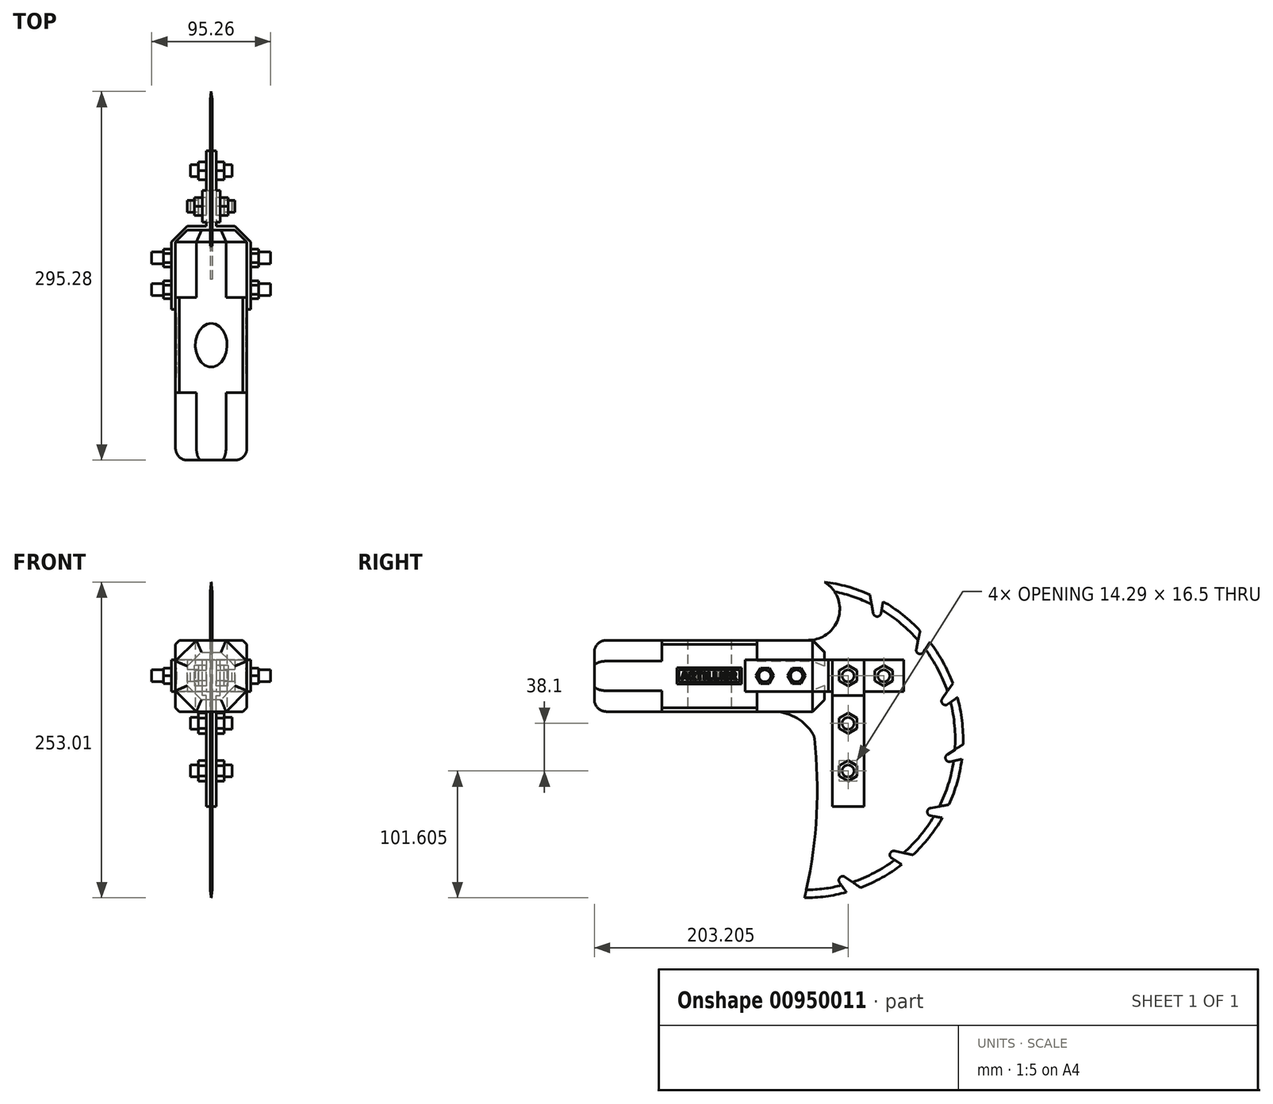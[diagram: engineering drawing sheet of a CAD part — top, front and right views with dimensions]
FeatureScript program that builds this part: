
annotation { "Feature Type Name" : "Feature", "Feature Type Description" : "" }
export const myFeature = defineFeature(function(context is Context, id is Id, definition is map)
    precondition{}
    {
        {
            var Q0;
            Q0=qCreatedBy(makeId("Top.planeOp"),FACE);
            var sketch = newSketch(context, id + "F0", { "sketchPlane" : qUnion([Q0])});
            skEllipse(sketch, "E0", {"center": v(0, 0) * mm, "majorRadius": 12.7 * mm, "minorRadius": 17.46 * mm, "majorAxis": v(1, 0)});
            skSolve(sketch);
        }
        {
            var Q0;
            Q0 = qSketchRegion(id + "F0", true);
            extrude(context, id + "F1", {"entities" : qUnion([Q0]), "depth" : 1219.2 * mm, "offsetDistance" : 25.4 * mm});
        }
        {
            var Q0;
            Q0=qCreatedBy(makeId("Front.planeOp"),FACE);
            var sketch = newSketch(context, id + "F2", { "sketchPlane" : qUnion([Q0])});
            skCircle(sketch, "E1.cCircle", {"center": v(0, 1177.87) * mm, "radius": 30.93 * mm, "construction": true});
            skLineSegment(sketch, "E1.0", {"start": v(28.57, 1189.7) * mm, "end": v(28.57, 1166.03) * mm});
            skLineSegment(sketch, "E1.1", {"start": v(28.57, 1166.03) * mm, "end": v(11.84, 1149.3) * mm});
            skLineSegment(sketch, "E1.2", {"start": v(11.84, 1149.3) * mm, "end": v(-11.84, 1149.3) * mm});
            skLineSegment(sketch, "E1.3", {"start": v(-11.84, 1149.3) * mm, "end": v(-28.58, 1166.03) * mm});
            skLineSegment(sketch, "E1.4", {"start": v(-28.58, 1166.03) * mm, "end": v(-28.58, 1189.7) * mm});
            skLineSegment(sketch, "E1.5", {"start": v(-28.57, 1189.7) * mm, "end": v(-11.84, 1206.44) * mm});
            skLineSegment(sketch, "E1.6", {"start": v(-11.84, 1206.44) * mm, "end": v(11.84, 1206.44) * mm});
            skLineSegment(sketch, "E1.7", {"start": v(11.84, 1206.44) * mm, "end": v(28.57, 1189.7) * mm});
            skLineSegment(sketch, "E2.bottom", {"start": v(28.57, 1206.44) * mm, "end": v(-28.58, 1206.44) * mm});
            skLineSegment(sketch, "E2.top", {"start": v(28.57, 1149.3) * mm, "end": v(-28.58, 1149.3) * mm});
            skLineSegment(sketch, "E2.left", {"start": v(28.57, 1206.44) * mm, "end": v(28.57, 1149.3) * mm});
            skLineSegment(sketch, "E2.right", {"start": v(-28.58, 1206.44) * mm, "end": v(-28.58, 1149.3) * mm});
            skSolve(sketch);
        }
        {
            var Q0;
            {var subQ0=sQuery(id+"F2.wireOp",EDGE,"E1.5");Q0=makeQuery(id+"F2.imprint","IMPRINT",FACE,{"disambiguationData":[TD([[makeQuery(id+"F2.imprint","IMPRINT",EDGE,{"derivedFrom":subQ0}),1.0]])]});}
            var Q1;
            {var subQ0=sQuery(id+"F2.wireOp",EDGE,"E1.7");Q1=makeQuery(id+"F2.imprint","IMPRINT",FACE,{"disambiguationData":[TD([[makeQuery(id+"F2.imprint","IMPRINT",EDGE,{"derivedFrom":subQ0}),1.0]])]});}
            var Q2;
            Q2=makeQuery(id+"F2.imprint","IMPRINT",FACE,{"disambiguationData":[TD([[makeQuery(id+"F2.imprint","IMPRINT",EDGE,{"derivedFrom":sQuery(id+"F2.wireOp",EDGE,"E1.0")}),-1.0]])]});
            var Q3;
            {var subQ0=sQuery(id+"F2.wireOp",EDGE,"E1.3");Q3=makeQuery(id+"F2.imprint","IMPRINT",FACE,{"disambiguationData":[TD([[makeQuery(id+"F2.imprint","IMPRINT",EDGE,{"derivedFrom":subQ0}),1.0]])]});}
            var Q4;
            {var subQ0=sQuery(id+"F2.wireOp",EDGE,"E1.1");Q4=makeQuery(id+"F2.imprint","IMPRINT",FACE,{"disambiguationData":[TD([[makeQuery(id+"F2.imprint","IMPRINT",EDGE,{"derivedFrom":subQ0}),1.0]])]});}
            extrude(context, id + "F3", {"entities" : qUnion([Q0, Q1, Q2, Q3, Q4]), "depth" : 38.1 * mm, "offsetDistance" : 25.4 * mm, "hasSecondDirection" : true, "secondDirectionOppositeDirection" : true, "secondDirectionDepth" : 38.1 * mm});
        }
        {
            var Q0;
            Q0=makeQuery(id+"F2.imprint","IMPRINT",FACE,{"disambiguationData":[TD([[makeQuery(id+"F2.imprint","IMPRINT",EDGE,{"derivedFrom":sQuery(id+"F2.wireOp",EDGE,"E1.0")}),-1.0]])]});
            extrude(context, id + "F4", {"entities" : qUnion([Q0]), "operationType" : NewBodyOperationType.ADD, "depth" : 92.07 * mm, "offsetDistance" : 25.4 * mm, "hasSecondDirection" : true, "secondDirectionOppositeDirection" : true, "secondDirectionDepth" : 92.07 * mm});
        }
        {
            var Q0;
            Q0=makeQuery(id+"F4.opExtrude","CAP_EDGE",EDGE,{"disambiguationData":[OSD([sQuery(id+"F2.wireOp",EDGE,"E1.1")])],"isStart":true});
            var Q1;
            Q1=makeQuery(id+"F4.opExtrude","CAP_EDGE",EDGE,{"disambiguationData":[OSD([sQuery(id+"F2.wireOp",EDGE,"E1.0")])],"isStart":true});
            var Q2;
            Q2=makeQuery(id+"F4.opExtrude","CAP_EDGE",EDGE,{"disambiguationData":[OSD([sQuery(id+"F2.wireOp",EDGE,"E1.7")])],"isStart":true});
            var Q3;
            Q3=makeQuery(id+"F4.opExtrude","CAP_EDGE",EDGE,{"disambiguationData":[OSD([sQuery(id+"F2.wireOp",EDGE,"E1.3")])],"isStart":true});
            var Q4;
            Q4=makeQuery(id+"F4.opExtrude","CAP_EDGE",EDGE,{"disambiguationData":[OSD([sQuery(id+"F2.wireOp",EDGE,"E1.5")])],"isStart":true});
            var Q5;
            Q5=makeQuery(id+"F4.opExtrude","CAP_EDGE",EDGE,{"disambiguationData":[OSD([sQuery(id+"F2.wireOp",EDGE,"E1.4")])],"isStart":true});
            var Q6;
            Q6=makeQuery(id+"F4.opExtrude","CAP_EDGE",EDGE,{"disambiguationData":[OSD([sQuery(id+"F2.wireOp",EDGE,"E1.6")])],"isStart":true});
            var Q7;
            Q7=makeQuery(id+"F4.opExtrude","CAP_EDGE",EDGE,{"disambiguationData":[OSD([sQuery(id+"F2.wireOp",EDGE,"E1.2")])],"isStart":true});
            chamfer(context, id + "F5", {"entities" : qUnion([Q0, Q1, Q2, Q3, Q4, Q5, Q6, Q7]), "width" : 9.52 * mm, "tangentPropagation" : true});
        }
        {
            var Q0;
            Q0=makeQuery(id+"F4.opExtrude","CAP_FACE",FACE,{"disambiguationData":[OSD([sQuery(id+"F2.wireOp",EDGE,"E1.0"),sQuery(id+"F2.wireOp",EDGE,"E1.1"),sQuery(id+"F2.wireOp",EDGE,"E1.2"),sQuery(id+"F2.wireOp",EDGE,"E1.3"),sQuery(id+"F2.wireOp",EDGE,"E1.4"),sQuery(id+"F2.wireOp",EDGE,"E1.5"),sQuery(id+"F2.wireOp",EDGE,"E1.6"),sQuery(id+"F2.wireOp",EDGE,"E1.7")])],"isStart":false});
            fillet(context, id + "F6", {"entities" : qUnion([Q0]), "radius" : 9.52 * mm, "tangentPropagation" : true, "allowEdgeOverflow" : false});
        }
        {
            var Q0;
            Q0=qCreatedBy(makeId("Right.planeOp"),FACE);
            var sketch = newSketch(context, id + "F7", { "sketchPlane" : qUnion([Q0])});
            skPoint(sketch, "E3", {"position": v(38.1, 1177.93) * mm});
            skPoint(sketch, "E4", {"position": v(92.07, 1177.93) * mm});
            skCircle(sketch, "E5", {"center": v(76.2, 1127.13) * mm, "radius": 127 * mm});
            skCircle(sketch, "E6", {"center": v(76.2, 1127.13) * mm, "radius": 7.94 * mm});
            skLineSegment(sketch, "E7.bottom", {"start": v(38.1, 1149.35) * mm, "end": v(82.55, 1149.35) * mm});
            skLineSegment(sketch, "E7.top", {"start": v(38.1, 1206.5) * mm, "end": v(82.55, 1206.5) * mm});
            skLineSegment(sketch, "E7.left", {"start": v(38.1, 1149.35) * mm, "end": v(38.1, 1206.5) * mm});
            skLineSegment(sketch, "E7.right", {"start": v(92.07, 1149.35) * mm, "end": v(92.07, 1206.5) * mm});
            skPoint(sketch, "E7.middle", {"position": v(65.09, 1177.93) * mm});
            skArc(sketch, "E8", {"start": v(79.37, 1206.5) * mm, "mid": v(103.54, 1224.96) * mm, "end": v(92.07, 1253.13) * mm});
            skArc(sketch, "E9", {"start": v(82.98, 1131.25) * mm, "mid": v(69.26, 1144.51) * mm, "end": v(50.8, 1149.35) * mm});
            skArc(sketch, "E10", {"start": v(76.2, 1000.13) * mm, "mid": v(85.65, 1063.72) * mm, "end": v(84.09, 1128) * mm});
            skLineSegment(sketch, "E11", {"start": v(76.2, 1127.13) * mm, "end": v(92.07, 1253.13) * mm, "construction": true});
            skLineSegment(sketch, "E12", {"start": v(76.2, 1127.13) * mm, "end": v(139.09, 1237.46) * mm, "construction": true});
            skLineSegment(sketch, "E13", {"start": v(76.2, 1127.13) * mm, "end": v(176.52, 1205) * mm, "construction": true});
            skLineSegment(sketch, "E14", {"start": v(76.2, 1127.13) * mm, "end": v(198.69, 1160.68) * mm, "construction": true});
            skLineSegment(sketch, "E15", {"start": v(76.2, 1127.13) * mm, "end": v(202.2, 1111.25) * mm, "construction": true});
            skLineSegment(sketch, "E16", {"start": v(76.2, 1127.13) * mm, "end": v(186.54, 1064.24) * mm, "construction": true});
            skLineSegment(sketch, "E17", {"start": v(76.2, 1127.13) * mm, "end": v(154.07, 1026.8) * mm, "construction": true});
            skLineSegment(sketch, "E18", {"start": v(109.75, 1004.64) * mm, "end": v(76.2, 1127.13) * mm, "construction": true});
            skLineSegment(sketch, "E19", {"start": v(139.09, 1237.46) * mm, "end": v(137.48, 1228.07) * mm});
            skLineSegment(sketch, "E20", {"start": v(176.52, 1205) * mm, "end": v(171.45, 1196.94) * mm});
            skLineSegment(sketch, "E21", {"start": v(198.69, 1160.68) * mm, "end": v(190.92, 1155.17) * mm});
            skLineSegment(sketch, "E22", {"start": v(202.2, 1111.25) * mm, "end": v(192.92, 1109.14) * mm});
            skLineSegment(sketch, "E23", {"start": v(186.54, 1064.24) * mm, "end": v(177.15, 1065.84) * mm});
            skLineSegment(sketch, "E24", {"start": v(154.07, 1026.8) * mm, "end": v(146.01, 1031.87) * mm});
            skLineSegment(sketch, "E25", {"start": v(109.75, 1004.64) * mm, "end": v(104.25, 1012.4) * mm});
            skArc(sketch, "E26", {"start": v(137.48, 1228.07) * mm, "mid": v(134.37, 1225.43) * mm, "end": v(131.23, 1228.04) * mm});
            skLineSegment(sketch, "E27", {"start": v(131.23, 1228.04) * mm, "end": v(128.54, 1242.84) * mm});
            skArc(sketch, "E28", {"start": v(171.45, 1196.94) * mm, "mid": v(167.56, 1195.69) * mm, "end": v(165.66, 1199.3) * mm});
            skLineSegment(sketch, "E29", {"start": v(165.66, 1199.3) * mm, "end": v(168.83, 1214) * mm});
            skArc(sketch, "E30", {"start": v(190.92, 1155.17) * mm, "mid": v(186.85, 1155.5) * mm, "end": v(186.47, 1159.57) * mm});
            skLineSegment(sketch, "E31", {"start": v(186.47, 1159.57) * mm, "end": v(195.03, 1171.94) * mm});
            skArc(sketch, "E32", {"start": v(192.92, 1109.14) * mm, "mid": v(189.29, 1111) * mm, "end": v(190.5, 1114.9) * mm});
            skLineSegment(sketch, "E33", {"start": v(190.5, 1114.9) * mm, "end": v(203.13, 1123.06) * mm});
            skArc(sketch, "E34", {"start": v(177.15, 1065.84) * mm, "mid": v(174.5, 1068.95) * mm, "end": v(177.11, 1072.1) * mm});
            skArc(sketch, "E35", {"start": v(146.01, 1031.87) * mm, "mid": v(144.76, 1035.76) * mm, "end": v(148.37, 1037.67) * mm});
            skArc(sketch, "E36", {"start": v(104.25, 1012.4) * mm, "mid": v(104.58, 1016.48) * mm, "end": v(108.64, 1016.86) * mm});
            skLineSegment(sketch, "E37", {"start": v(108.64, 1016.86) * mm, "end": v(121.02, 1008.3) * mm});
            skLineSegment(sketch, "E38", {"start": v(148.37, 1037.67) * mm, "end": v(163.08, 1034.5) * mm});
            skLineSegment(sketch, "E39", {"start": v(177.11, 1072.1) * mm, "end": v(191.91, 1074.79) * mm});
            skLineSegment(sketch, "E40", {"start": v(82.55, 1206.5) * mm, "end": v(92.07, 1196.98) * mm});
            skLineSegment(sketch, "E41", {"start": v(82.55, 1149.35) * mm, "end": v(92.08, 1158.88) * mm});
            skSolve(sketch);
        }
        {
            var Q0;
            {var subQ9=sQuery(id+"F7.wireOp",EDGE,"E8");Q0=makeQuery(id+"F7.imprint","IMPRINT",FACE,{"disambiguationData":[TD([[makeQuery(id+"F7.imprint","IMPRINT",EDGE,{"derivedFrom":subQ9}),-1.0]])]});}
            extrude(context, id + "F8", {"entities" : qUnion([Q0]), "depth" : 0.8 * mm, "offsetDistance" : 25.4 * mm, "hasSecondDirection" : true, "secondDirectionOppositeDirection" : true, "secondDirectionDepth" : 0.8 * mm});
        }
        {
            var Q0;
            {var subQ0=sQuery(id+"F7.wireOp",EDGE,"E5");Q0=makeQuery(id+"F8.opExtrude","CAP_EDGE",EDGE,{"disambiguationData":[OSD([subQ0]),TDD([makeQuery(id+"F7.imprint","IMPRINT",EDGE,{"disambiguationData":[TD([[makeQuery(id+"F7.imprint","INTERSECT",VERTEX,{"derivedFrom":[subQ0,sQuery(id+"F7.wireOp",EDGE,"E10")]}),-1.0]])],"derivedFrom":subQ0})])],"isStart":true});}
            var Q1;
            {var subQ0=sQuery(id+"F7.wireOp",EDGE,"E5");Q1=makeQuery(id+"F8.opExtrude","CAP_EDGE",EDGE,{"disambiguationData":[OSD([subQ0]),TDD([makeQuery(id+"F7.imprint","IMPRINT",EDGE,{"disambiguationData":[TD([[makeQuery(id+"F7.imprint","INTERSECT",VERTEX,{"derivedFrom":[subQ0,sQuery(id+"F7.wireOp",EDGE,"E22")]}),1.0]])],"derivedFrom":subQ0})])],"isStart":true});}
            var Q2;
            {var subQ0=sQuery(id+"F7.wireOp",EDGE,"E5");Q2=makeQuery(id+"F8.opExtrude","CAP_EDGE",EDGE,{"disambiguationData":[OSD([subQ0]),TDD([makeQuery(id+"F7.imprint","IMPRINT",EDGE,{"disambiguationData":[TD([[makeQuery(id+"F7.imprint","INTERSECT",VERTEX,{"derivedFrom":[subQ0,sQuery(id+"F7.wireOp",EDGE,"E21")]}),1.0]])],"derivedFrom":subQ0})])],"isStart":true});}
            var Q3;
            {var subQ0=sQuery(id+"F7.wireOp",EDGE,"E5");Q3=makeQuery(id+"F8.opExtrude","CAP_EDGE",EDGE,{"disambiguationData":[OSD([subQ0]),TDD([makeQuery(id+"F7.imprint","IMPRINT",EDGE,{"disambiguationData":[TD([[makeQuery(id+"F7.imprint","INTERSECT",VERTEX,{"derivedFrom":[subQ0,sQuery(id+"F7.wireOp",EDGE,"E20")]}),1.0]])],"derivedFrom":subQ0})])],"isStart":true});}
            var Q4;
            {var subQ0=sQuery(id+"F7.wireOp",EDGE,"E5");Q4=makeQuery(id+"F8.opExtrude","CAP_EDGE",EDGE,{"disambiguationData":[OSD([subQ0]),TDD([makeQuery(id+"F7.imprint","IMPRINT",EDGE,{"disambiguationData":[TD([[makeQuery(id+"F7.imprint","INTERSECT",VERTEX,{"derivedFrom":[subQ0,sQuery(id+"F7.wireOp",EDGE,"E19")]}),1.0]])],"derivedFrom":subQ0})])],"isStart":true});}
            var Q5;
            {var subQ0=sQuery(id+"F7.wireOp",EDGE,"E5");Q5=makeQuery(id+"F8.opExtrude","CAP_EDGE",EDGE,{"disambiguationData":[OSD([subQ0]),TDD([makeQuery(id+"F7.imprint","IMPRINT",EDGE,{"disambiguationData":[TD([[makeQuery(id+"F7.imprint","INTERSECT",VERTEX,{"derivedFrom":[subQ0,sQuery(id+"F7.wireOp",EDGE,"E8")]}),1.0]])],"derivedFrom":subQ0})])],"isStart":true});}
            var Q6;
            {var subQ0=sQuery(id+"F7.wireOp",EDGE,"E5");Q6=makeQuery(id+"F8.opExtrude","CAP_EDGE",EDGE,{"disambiguationData":[OSD([subQ0]),TDD([makeQuery(id+"F7.imprint","IMPRINT",EDGE,{"disambiguationData":[TD([[makeQuery(id+"F7.imprint","INTERSECT",VERTEX,{"derivedFrom":[subQ0,sQuery(id+"F7.wireOp",EDGE,"E24")]}),1.0]])],"derivedFrom":subQ0})])],"isStart":true});}
            var Q7;
            {var subQ0=sQuery(id+"F7.wireOp",EDGE,"E5");Q7=makeQuery(id+"F8.opExtrude","CAP_EDGE",EDGE,{"disambiguationData":[OSD([subQ0]),TDD([makeQuery(id+"F7.imprint","IMPRINT",EDGE,{"disambiguationData":[TD([[makeQuery(id+"F7.imprint","INTERSECT",VERTEX,{"derivedFrom":[subQ0,sQuery(id+"F7.wireOp",EDGE,"E23")]}),1.0]])],"derivedFrom":subQ0})])],"isStart":true});}
            chamfer(context, id + "F9", {"entities" : qUnion([Q0, Q1, Q2, Q3, Q4, Q5, Q6, Q7]), "chamferType" : ChamferType.TWO_OFFSETS, "width1" : 0.8 * mm, "oppositeDirection" : false, "width2" : 6.35 * mm, "tangentPropagation" : true});
        }
        {
            var Q0;
            {var subQ0=sQuery(id+"F7.wireOp",EDGE,"E5");Q0=makeQuery(id+"F8.opExtrude","CAP_EDGE",EDGE,{"disambiguationData":[OSD([subQ0]),TDD([makeQuery(id+"F7.imprint","IMPRINT",EDGE,{"disambiguationData":[TD([[makeQuery(id+"F7.imprint","INTERSECT",VERTEX,{"derivedFrom":[subQ0,sQuery(id+"F7.wireOp",EDGE,"E10")]}),-1.0]])],"derivedFrom":subQ0})])],"isStart":false});}
            var Q1;
            {var subQ0=sQuery(id+"F7.wireOp",EDGE,"E5");Q1=makeQuery(id+"F8.opExtrude","CAP_EDGE",EDGE,{"disambiguationData":[OSD([subQ0]),TDD([makeQuery(id+"F7.imprint","IMPRINT",EDGE,{"disambiguationData":[TD([[makeQuery(id+"F7.imprint","INTERSECT",VERTEX,{"derivedFrom":[subQ0,sQuery(id+"F7.wireOp",EDGE,"E23")]}),1.0]])],"derivedFrom":subQ0})])],"isStart":false});}
            var Q2;
            {var subQ0=sQuery(id+"F7.wireOp",EDGE,"E5");Q2=makeQuery(id+"F8.opExtrude","CAP_EDGE",EDGE,{"disambiguationData":[OSD([subQ0]),TDD([makeQuery(id+"F7.imprint","IMPRINT",EDGE,{"disambiguationData":[TD([[makeQuery(id+"F7.imprint","INTERSECT",VERTEX,{"derivedFrom":[subQ0,sQuery(id+"F7.wireOp",EDGE,"E22")]}),1.0]])],"derivedFrom":subQ0})])],"isStart":false});}
            var Q3;
            {var subQ0=sQuery(id+"F7.wireOp",EDGE,"E5");Q3=makeQuery(id+"F8.opExtrude","CAP_EDGE",EDGE,{"disambiguationData":[OSD([subQ0]),TDD([makeQuery(id+"F7.imprint","IMPRINT",EDGE,{"disambiguationData":[TD([[makeQuery(id+"F7.imprint","INTERSECT",VERTEX,{"derivedFrom":[subQ0,sQuery(id+"F7.wireOp",EDGE,"E21")]}),1.0]])],"derivedFrom":subQ0})])],"isStart":false});}
            var Q4;
            {var subQ0=sQuery(id+"F7.wireOp",EDGE,"E5");Q4=makeQuery(id+"F8.opExtrude","CAP_EDGE",EDGE,{"disambiguationData":[OSD([subQ0]),TDD([makeQuery(id+"F7.imprint","IMPRINT",EDGE,{"disambiguationData":[TD([[makeQuery(id+"F7.imprint","INTERSECT",VERTEX,{"derivedFrom":[subQ0,sQuery(id+"F7.wireOp",EDGE,"E20")]}),1.0]])],"derivedFrom":subQ0})])],"isStart":false});}
            var Q5;
            {var subQ0=sQuery(id+"F7.wireOp",EDGE,"E5");Q5=makeQuery(id+"F8.opExtrude","CAP_EDGE",EDGE,{"disambiguationData":[OSD([subQ0]),TDD([makeQuery(id+"F7.imprint","IMPRINT",EDGE,{"disambiguationData":[TD([[makeQuery(id+"F7.imprint","INTERSECT",VERTEX,{"derivedFrom":[subQ0,sQuery(id+"F7.wireOp",EDGE,"E19")]}),1.0]])],"derivedFrom":subQ0})])],"isStart":false});}
            var Q6;
            {var subQ0=sQuery(id+"F7.wireOp",EDGE,"E5");Q6=makeQuery(id+"F8.opExtrude","CAP_EDGE",EDGE,{"disambiguationData":[OSD([subQ0]),TDD([makeQuery(id+"F7.imprint","IMPRINT",EDGE,{"disambiguationData":[TD([[makeQuery(id+"F7.imprint","INTERSECT",VERTEX,{"derivedFrom":[subQ0,sQuery(id+"F7.wireOp",EDGE,"E8")]}),1.0]])],"derivedFrom":subQ0})])],"isStart":false});}
            var Q7;
            {var subQ0=sQuery(id+"F7.wireOp",EDGE,"E5");Q7=makeQuery(id+"F8.opExtrude","CAP_EDGE",EDGE,{"disambiguationData":[OSD([subQ0]),TDD([makeQuery(id+"F7.imprint","IMPRINT",EDGE,{"disambiguationData":[TD([[makeQuery(id+"F7.imprint","INTERSECT",VERTEX,{"derivedFrom":[subQ0,sQuery(id+"F7.wireOp",EDGE,"E24")]}),1.0]])],"derivedFrom":subQ0})])],"isStart":false});}
            chamfer(context, id + "F10", {"entities" : qUnion([Q0, Q1, Q2, Q3, Q4, Q5, Q6, Q7]), "chamferType" : ChamferType.TWO_OFFSETS, "width1" : 0.8 * mm, "oppositeDirection" : true, "width2" : 6.35 * mm, "tangentPropagation" : true});
        }
        {
            var Q0;
            Q0=makeQuery(id+"F3.opExtrude","SWEPT_EDGE",EDGE,{"disambiguationData":[OSD([sQuery(id+"F2.wireOp",EDGE,"E2.bottom"),sQuery(id+"F2.wireOp",EDGE,"E2.left")])]});
            var Q1;
            Q1=makeQuery(id+"F3.opExtrude","SWEPT_EDGE",EDGE,{"disambiguationData":[OSD([sQuery(id+"F2.wireOp",EDGE,"E2.top"),sQuery(id+"F2.wireOp",EDGE,"E2.left")])]});
            var Q2;
            Q2=makeQuery(id+"F3.opExtrude","SWEPT_EDGE",EDGE,{"disambiguationData":[OSD([sQuery(id+"F2.wireOp",EDGE,"E2.bottom"),sQuery(id+"F2.wireOp",EDGE,"E2.right")])]});
            var Q3;
            Q3=makeQuery(id+"F3.opExtrude","SWEPT_EDGE",EDGE,{"disambiguationData":[OSD([sQuery(id+"F2.wireOp",EDGE,"E2.top"),sQuery(id+"F2.wireOp",EDGE,"E2.right")])]});
            chamfer(context, id + "F11", {"entities" : qUnion([Q0, Q1, Q2, Q3]), "width" : 3.17 * mm, "tangentPropagation" : true});
        }
        {
            var Q0;
            Q0 = qSketchRegion(id + "F0", true);
            extrude(context, id + "F12", {"entities" : qUnion([Q0]), "operationType" : NewBodyOperationType.REMOVE, "depth" : 1219.2 * mm, "offsetDistance" : 25.4 * mm});
        }
        {
            var Q0;
            Q0=qCreatedBy(makeId("Top.planeOp"),FACE);
            var sketch = newSketch(context, id + "F13", { "sketchPlane" : qUnion([Q0])});
            skLineSegment(sketch, "E42.bottom", {"start": v(28.58, 28.58) * mm, "end": v(31.75, 28.58) * mm});
            skLineSegment(sketch, "E42.top", {"start": v(28.57, 82.55) * mm, "end": v(31.75, 82.55) * mm, "construction": true});
            skLineSegment(sketch, "E42.left", {"start": v(28.58, 28.58) * mm, "end": v(28.57, 82.55) * mm});
            skLineSegment(sketch, "E42.right", {"start": v(31.75, 28.58) * mm, "end": v(31.75, 82.55) * mm});
            skLineSegment(sketch, "E43", {"start": v(28.57, 82.55) * mm, "end": v(19.05, 92.08) * mm});
            skLineSegment(sketch, "E44", {"start": v(19.05, 92.08) * mm, "end": v(0.8, 92.08) * mm});
            skLineSegment(sketch, "E45", {"start": v(0.8, 92.08) * mm, "end": v(0.8, 155.58) * mm});
            skLineSegment(sketch, "E46", {"start": v(0.8, 155.58) * mm, "end": v(3.97, 155.58) * mm});
            skLineSegment(sketch, "E47", {"start": v(3.97, 155.58) * mm, "end": v(3.97, 95.25) * mm});
            skLineSegment(sketch, "E48", {"start": v(3.97, 95.25) * mm, "end": v(19.05, 95.25) * mm});
            skLineSegment(sketch, "E49", {"start": v(19.05, 95.25) * mm, "end": v(31.75, 82.55) * mm});
            skLineSegment(sketch, "E50", {"start": v(0, 165.18) * mm, "end": v(0, 0) * mm, "construction": true});
            skLineSegment(sketch, "E51.MirrorCS", {"start": v(-31.75, 28.58) * mm, "end": v(-31.75, 82.55) * mm});
            skLineSegment(sketch, "E52.MirrorCS", {"start": v(-28.58, 28.58) * mm, "end": v(-28.57, 82.55) * mm});
            skLineSegment(sketch, "E53.MirrorCS", {"start": v(-28.57, 28.58) * mm, "end": v(-31.75, 28.58) * mm});
            skLineSegment(sketch, "E54.MirrorCS", {"start": v(-28.57, 82.55) * mm, "end": v(-19.05, 92.08) * mm});
            skLineSegment(sketch, "E55.MirrorCS", {"start": v(-19.05, 95.25) * mm, "end": v(-31.75, 82.55) * mm});
            skLineSegment(sketch, "E56.MirrorCS", {"start": v(-3.97, 95.25) * mm, "end": v(-19.05, 95.25) * mm});
            skLineSegment(sketch, "E57.MirrorCS", {"start": v(-19.05, 92.08) * mm, "end": v(-0.8, 92.08) * mm});
            skLineSegment(sketch, "E58.MirrorCS", {"start": v(-3.97, 155.58) * mm, "end": v(-3.97, 95.25) * mm});
            skLineSegment(sketch, "E59.MirrorCS", {"start": v(-0.8, 92.08) * mm, "end": v(-0.8, 155.58) * mm});
            skLineSegment(sketch, "E60.MirrorCS", {"start": v(-0.8, 155.58) * mm, "end": v(-3.97, 155.58) * mm});
            skSolve(sketch);
        }
        {
            var Q0;
            Q0=makeQuery(id+"F13.imprint","IMPRINT",FACE,{"disambiguationData":[TD([[makeQuery(id+"F13.imprint","IMPRINT",EDGE,{"derivedFrom":sQuery(id+"F13.wireOp",EDGE,"E51.MirrorCS")}),-1.0]])]});
            var Q1;
            Q1=makeQuery(id+"F13.imprint","IMPRINT",FACE,{"disambiguationData":[TD([[makeQuery(id+"F13.imprint","IMPRINT",EDGE,{"derivedFrom":sQuery(id+"F13.wireOp",EDGE,"E42.bottom")}),1.0]])]});
            extrude(context, id + "F14", {"entities" : qUnion([Q0, Q1]), "operationType" : NewBodyOperationType.ADD, "depth" : 1190.62 * mm, "offsetDistance" : 25.4 * mm, "hasSecondDirection" : true, "secondDirectionOppositeDirection" : false, "secondDirectionDepth" : 1165.22 * mm});
        }
        {
            var Q0;
            Q0=qCreatedBy(makeId("Front.planeOp"),FACE);
            var sketch = newSketch(context, id + "F15", { "sketchPlane" : qUnion([Q0])});
            skLineSegment(sketch, "E61", {"start": v(3.97, 1190.62) * mm, "end": v(3.97, 1165.22) * mm});
            skLineSegment(sketch, "E62", {"start": v(3.97, 1165.22) * mm, "end": v(0.8, 1165.22) * mm});
            skLineSegment(sketch, "E63", {"start": v(0.8, 1165.22) * mm, "end": v(0.8, 1073.15) * mm});
            skLineSegment(sketch, "E64", {"start": v(0.8, 1073.15) * mm, "end": v(3.97, 1073.15) * mm});
            skLineSegment(sketch, "E65", {"start": v(3.97, 1073.15) * mm, "end": v(3.97, 1162.05) * mm});
            skLineSegment(sketch, "E66", {"start": v(3.97, 1162.05) * mm, "end": v(7.14, 1162.05) * mm});
            skLineSegment(sketch, "E67", {"start": v(7.14, 1162.05) * mm, "end": v(7.14, 1190.62) * mm});
            skLineSegment(sketch, "E68", {"start": v(7.14, 1190.62) * mm, "end": v(7.14, 1190.62) * mm});
            skLineSegment(sketch, "E69", {"start": v(7.14, 1190.62) * mm, "end": v(3.97, 1190.62) * mm});
            skLineSegment(sketch, "E70", {"start": v(0, 1190.62) * mm, "end": v(0, 1073.15) * mm, "construction": true});
            skLineSegment(sketch, "E71.MirrorCS", {"start": v(-0.8, 1165.22) * mm, "end": v(-0.8, 1073.15) * mm});
            skLineSegment(sketch, "E72.MirrorCS", {"start": v(-0.8, 1073.15) * mm, "end": v(-3.97, 1073.15) * mm});
            skLineSegment(sketch, "E73.MirrorCS", {"start": v(-3.97, 1073.15) * mm, "end": v(-3.97, 1162.05) * mm});
            skLineSegment(sketch, "E74.MirrorCS", {"start": v(-3.97, 1165.22) * mm, "end": v(-0.8, 1165.22) * mm});
            skLineSegment(sketch, "E75.MirrorCS", {"start": v(-3.97, 1162.05) * mm, "end": v(-7.14, 1162.05) * mm});
            skLineSegment(sketch, "E76.MirrorCS", {"start": v(-7.14, 1162.05) * mm, "end": v(-7.14, 1190.62) * mm});
            skLineSegment(sketch, "E77.MirrorCS", {"start": v(-3.97, 1190.62) * mm, "end": v(-3.97, 1165.22) * mm});
            skLineSegment(sketch, "E78.MirrorCS", {"start": v(-7.14, 1190.62) * mm, "end": v(-3.97, 1190.62) * mm});
            skSolve(sketch);
        }
        {
            var Q0;
            Q0 = qSketchRegion(id + "F15", true);
            extrude(context, id + "F16", {"entities" : qUnion([Q0]), "operationType" : NewBodyOperationType.ADD, "oppositeDirection" : true, "depth" : 123.82 * mm, "offsetDistance" : 25.4 * mm, "hasSecondDirection" : true, "secondDirectionOppositeDirection" : true, "secondDirectionDepth" : 98.42 * mm});
        }
        {
            var Q0;
            Q0=qCreatedBy(makeId("Right.planeOp"),FACE);
            var sketch = newSketch(context, id + "F17", { "sketchPlane" : qUnion([Q0])});
            skCircle(sketch, "E79.cCircle", {"center": v(111.12, 1177.93) * mm, "radius": 7.14 * mm, "construction": true});
            skLineSegment(sketch, "E79.0", {"start": v(118.27, 1182.05) * mm, "end": v(118.27, 1173.8) * mm});
            skLineSegment(sketch, "E79.1", {"start": v(118.27, 1173.8) * mm, "end": v(111.12, 1169.68) * mm});
            skLineSegment(sketch, "E79.2", {"start": v(111.12, 1169.68) * mm, "end": v(103.98, 1173.8) * mm});
            skLineSegment(sketch, "E79.3", {"start": v(103.98, 1173.8) * mm, "end": v(103.98, 1182.05) * mm});
            skLineSegment(sketch, "E79.4", {"start": v(103.98, 1182.05) * mm, "end": v(111.12, 1186.17) * mm});
            skLineSegment(sketch, "E79.5", {"start": v(111.12, 1186.17) * mm, "end": v(118.27, 1182.05) * mm});
            skPoint(sketch, "E79.0.midPoint", {"position": v(118.27, 1177.93) * mm});
            skCircle(sketch, "E80", {"center": v(111.12, 1177.93) * mm, "radius": 4.76 * mm});
            skLineSegment(sketch, "E81.0.1.0", {"start": v(118.27, 1135.7) * mm, "end": v(111.12, 1131.58) * mm});
            skLineSegment(sketch, "E81.0.1.1", {"start": v(118.27, 1143.95) * mm, "end": v(118.27, 1135.7) * mm});
            skLineSegment(sketch, "E81.0.1.2", {"start": v(111.12, 1148.07) * mm, "end": v(118.27, 1143.95) * mm});
            skLineSegment(sketch, "E81.0.1.3", {"start": v(103.98, 1143.95) * mm, "end": v(111.12, 1148.07) * mm});
            skCircle(sketch, "E81.0.1.4", {"center": v(111.12, 1139.83) * mm, "radius": 4.76 * mm});
            skLineSegment(sketch, "E81.0.1.5", {"start": v(111.12, 1131.58) * mm, "end": v(103.98, 1135.7) * mm});
            skLineSegment(sketch, "E81.0.1.6", {"start": v(103.98, 1135.7) * mm, "end": v(103.98, 1143.95) * mm});
            skLineSegment(sketch, "E81.0.2.0", {"start": v(118.27, 1097.6) * mm, "end": v(111.12, 1093.48) * mm});
            skLineSegment(sketch, "E81.0.2.1", {"start": v(118.27, 1105.85) * mm, "end": v(118.27, 1097.6) * mm});
            skLineSegment(sketch, "E81.0.2.2", {"start": v(111.12, 1109.97) * mm, "end": v(118.27, 1105.85) * mm});
            skLineSegment(sketch, "E81.0.2.3", {"start": v(103.98, 1105.85) * mm, "end": v(111.12, 1109.97) * mm});
            skCircle(sketch, "E81.0.2.4", {"center": v(111.12, 1101.73) * mm, "radius": 4.76 * mm});
            skLineSegment(sketch, "E81.0.2.5", {"start": v(111.12, 1093.48) * mm, "end": v(103.98, 1097.6) * mm});
            skLineSegment(sketch, "E81.0.2.6", {"start": v(103.98, 1097.6) * mm, "end": v(103.98, 1105.85) * mm});
            skLineSegment(sketch, "E81.1.0.0", {"start": v(146.84, 1173.8) * mm, "end": v(139.7, 1169.68) * mm});
            skLineSegment(sketch, "E81.1.0.1", {"start": v(146.84, 1182.05) * mm, "end": v(146.84, 1173.8) * mm});
            skLineSegment(sketch, "E81.1.0.2", {"start": v(139.7, 1186.17) * mm, "end": v(146.84, 1182.05) * mm});
            skLineSegment(sketch, "E81.1.0.3", {"start": v(132.56, 1182.05) * mm, "end": v(139.7, 1186.17) * mm});
            skCircle(sketch, "E81.1.0.4", {"center": v(139.7, 1177.93) * mm, "radius": 4.76 * mm});
            skLineSegment(sketch, "E81.1.0.5", {"start": v(139.7, 1169.68) * mm, "end": v(132.56, 1173.8) * mm});
            skLineSegment(sketch, "E81.1.0.6", {"start": v(132.56, 1173.8) * mm, "end": v(132.56, 1182.05) * mm});
            skLineSegment(sketch, "E81.direction1", {"start": v(111.12, 1177.93) * mm, "end": v(139.7, 1177.93) * mm, "construction": true});
            skLineSegment(sketch, "E81.direction2", {"start": v(111.12, 1177.93) * mm, "end": v(111.12, 1139.83) * mm, "construction": true});
            skSolve(sketch);
        }
        {
            var Q0;
            Q0=makeQuery(id+"F17.imprint","IMPRINT",FACE,{"disambiguationData":[TD([[makeQuery(id+"F17.imprint","IMPRINT",EDGE,{"derivedFrom":sQuery(id+"F17.wireOp",EDGE,"E79.0")}),-1.0]])]});
            extrude(context, id + "F18", {"entities" : qUnion([Q0]), "operationType" : NewBodyOperationType.ADD, "depth" : 13.5 * mm, "offsetDistance" : 25.4 * mm, "hasSecondDirection" : true, "secondDirectionOppositeDirection" : true, "secondDirectionDepth" : 13.5 * mm});
        }
        {
            var Q0;
            Q0=makeQuery(id+"F17.imprint","IMPRINT",FACE,{"disambiguationData":[TD([[makeQuery(id+"F17.imprint","IMPRINT",EDGE,{"derivedFrom":sQuery(id+"F17.wireOp",EDGE,"E81.1.0.0")}),-1.0]])]});
            var Q1;
            Q1=makeQuery(id+"F17.imprint","IMPRINT",FACE,{"disambiguationData":[TD([[makeQuery(id+"F17.imprint","IMPRINT",EDGE,{"derivedFrom":sQuery(id+"F17.wireOp",EDGE,"E81.0.1.0")}),-1.0]])]});
            var Q2;
            Q2=makeQuery(id+"F17.imprint","IMPRINT",FACE,{"disambiguationData":[TD([[makeQuery(id+"F17.imprint","IMPRINT",EDGE,{"derivedFrom":sQuery(id+"F17.wireOp",EDGE,"E81.0.2.0")}),-1.0]])]});
            extrude(context, id + "F19", {"entities" : qUnion([Q0, Q1, Q2]), "operationType" : NewBodyOperationType.ADD, "depth" : 10.32 * mm, "offsetDistance" : 25.4 * mm, "hasSecondDirection" : true, "secondDirectionOppositeDirection" : true, "secondDirectionDepth" : 10.32 * mm});
        }
        {
            var Q0;
            Q0=makeQuery(id+"F17.imprint","IMPRINT",FACE,{"disambiguationData":[TD([[makeQuery(id+"F17.imprint","IMPRINT",EDGE,{"derivedFrom":sQuery(id+"F17.wireOp",EDGE,"E80")}),1.0]])]});
            extrude(context, id + "F20", {"entities" : qUnion([Q0]), "operationType" : NewBodyOperationType.ADD, "depth" : 19.08 * mm, "offsetDistance" : 25.4 * mm, "hasSecondDirection" : true, "secondDirectionOppositeDirection" : true, "secondDirectionDepth" : 19.08 * mm});
        }
        {
            var Q0;
            Q0=makeQuery(id+"F17.imprint","IMPRINT",FACE,{"disambiguationData":[TD([[makeQuery(id+"F17.imprint","IMPRINT",EDGE,{"derivedFrom":sQuery(id+"F17.wireOp",EDGE,"E81.1.0.4")}),1.0]])]});
            var Q1;
            Q1=makeQuery(id+"F17.imprint","IMPRINT",FACE,{"disambiguationData":[TD([[makeQuery(id+"F17.imprint","IMPRINT",EDGE,{"derivedFrom":sQuery(id+"F17.wireOp",EDGE,"E81.0.1.4")}),1.0]])]});
            var Q2;
            Q2=makeQuery(id+"F17.imprint","IMPRINT",FACE,{"disambiguationData":[TD([[makeQuery(id+"F17.imprint","IMPRINT",EDGE,{"derivedFrom":sQuery(id+"F17.wireOp",EDGE,"E81.0.2.4")}),1.0]])]});
            extrude(context, id + "F21", {"entities" : qUnion([Q0, Q1, Q2]), "operationType" : NewBodyOperationType.ADD, "depth" : 16.67 * mm, "offsetDistance" : 25.4 * mm, "hasSecondDirection" : true, "secondDirectionOppositeDirection" : true, "secondDirectionDepth" : 16.67 * mm});
        }
        {
            var Q0;
            {var subQ0=sQuery(id+"F2.wireOp",EDGE,"E1.0");Q0=makeQuery(id+"F4.boolean.opBoolean","MERGE",FACE,{"derivedFrom":[makeQuery(id+"F3.opExtrude","SWEPT_FACE",FACE,{"disambiguationData":[OSD([subQ0,sQuery(id+"F2.wireOp",EDGE,"E2.left")])]}),makeQuery(id+"F4.opExtrude","SWEPT_FACE",FACE,{"disambiguationData":[OSD([subQ0])]})]});}
            var sketch = newSketch(context, id + "F22", { "sketchPlane" : qUnion([Q0])});
            skLineSegment(sketch, "E82.bottom", {"start": v(28.57, 1162) * mm, "end": v(-28.58, 1162) * mm, "construction": true});
            skLineSegment(sketch, "E82.top", {"start": v(28.57, 1193.74) * mm, "end": v(-28.58, 1193.74) * mm, "construction": true});
            skLineSegment(sketch, "E82.left", {"start": v(28.57, 1162) * mm, "end": v(28.57, 1193.74) * mm, "construction": true});
            skLineSegment(sketch, "E82.right", {"start": v(-28.57, 1162) * mm, "end": v(-28.57, 1193.74) * mm, "construction": true});
            skPoint(sketch, "E82.middle", {"position": v(0, 1177.87) * mm});
            skLineSegment(sketch, "E83", {"start": v(0, 1193.74) * mm, "end": v(-28.58, 1177.87) * mm, "construction": true});
            skLineSegment(sketch, "E84", {"start": v(-28.57, 1177.87) * mm, "end": v(0, 1162) * mm, "construction": true});
            skLineSegment(sketch, "E85", {"start": v(0, 1162) * mm, "end": v(28.58, 1177.87) * mm, "construction": true});
            skLineSegment(sketch, "E86", {"start": v(28.58, 1177.87) * mm, "end": v(0, 1193.74) * mm, "construction": true});
            skLineSegment(sketch, "E87.bottom", {"start": v(24.29, 1173.01) * mm, "end": v(-24.29, 1173.01) * mm});
            skLineSegment(sketch, "E87.top", {"start": v(24.29, 1182.72) * mm, "end": v(-24.29, 1182.72) * mm});
            skLineSegment(sketch, "E87.left", {"start": v(24.29, 1173.01) * mm, "end": v(24.29, 1182.72) * mm});
            skLineSegment(sketch, "E87.right", {"start": v(-24.29, 1173.01) * mm, "end": v(-24.29, 1182.72) * mm});
            skLineSegment(sketch, "E88.bottom", {"start": v(25.87, 1171.43) * mm, "end": v(-25.87, 1171.43) * mm});
            skLineSegment(sketch, "E88.top", {"start": v(25.87, 1184.3) * mm, "end": v(-25.87, 1184.3) * mm});
            skLineSegment(sketch, "E88.left", {"start": v(25.87, 1171.43) * mm, "end": v(25.87, 1184.3) * mm});
            skLineSegment(sketch, "E88.right", {"start": v(-25.87, 1171.43) * mm, "end": v(-25.87, 1184.3) * mm});
            skPoint(sketch, "E89.sketch_text.left.end.orphan", {"position": v(-22.7, 1181.13) * mm});
            skPoint(sketch, "E90", {"position": v(22.7, 1181.13) * mm});
            skPoint(sketch, "E91", {"position": v(22.7, 1174.6) * mm});
            skPoint(sketch, "E92", {"position": v(-22.7, 1174.6) * mm});
            skText(sketch, "E93", { "text": "ARTILLIER", "fontName": "OpenSans-Bold.ttf"});
            const initialGuessF22  = {"E93": [-0.02283, 1.1746, 1, 0, 0.00655]};
            skSetInitialGuess(sketch, initialGuessF22);
            skSolve(sketch);
        }
        {
            var Q0;
            Q0=makeQuery(id+"F22.imprint","IMPRINT",FACE,{"disambiguationData":[TD([[makeQuery(id+"F22.imprint","IMPRINT",EDGE,{"derivedFrom":sQuery(id+"F22.wireOp",EDGE,"E93.sketch_text.stroke-0")}),-1.0]])]});
            var Q1;
            Q1=makeQuery(id+"F22.imprint","IMPRINT",FACE,{"disambiguationData":[TD([[makeQuery(id+"F22.imprint","IMPRINT",EDGE,{"derivedFrom":sQuery(id+"F22.wireOp",EDGE,"E93.sketch_text.stroke-12")}),-1.0]])]});
            var Q2;
            Q2=makeQuery(id+"F22.imprint","IMPRINT",FACE,{"disambiguationData":[TD([[makeQuery(id+"F22.imprint","IMPRINT",EDGE,{"derivedFrom":sQuery(id+"F22.wireOp",EDGE,"E93.sketch_text.stroke-31")}),-1.0]])]});
            var Q3;
            Q3=makeQuery(id+"F22.imprint","IMPRINT",FACE,{"disambiguationData":[TD([[makeQuery(id+"F22.imprint","IMPRINT",EDGE,{"derivedFrom":sQuery(id+"F22.wireOp",EDGE,"E93.sketch_text.stroke-39")}),-1.0]])]});
            var Q4;
            Q4=makeQuery(id+"F22.imprint","IMPRINT",FACE,{"disambiguationData":[TD([[makeQuery(id+"F22.imprint","IMPRINT",EDGE,{"derivedFrom":sQuery(id+"F22.wireOp",EDGE,"E93.sketch_text.stroke-43")}),-1.0]])]});
            var Q5;
            Q5=makeQuery(id+"F22.imprint","IMPRINT",FACE,{"disambiguationData":[TD([[makeQuery(id+"F22.imprint","IMPRINT",EDGE,{"derivedFrom":sQuery(id+"F22.wireOp",EDGE,"E87.bottom")}),1.0]])]});
            var Q6;
            Q6=makeQuery(id+"F22.imprint","IMPRINT",FACE,{"disambiguationData":[TD([[makeQuery(id+"F22.imprint","IMPRINT",EDGE,{"derivedFrom":sQuery(id+"F22.wireOp",EDGE,"E93.sketch_text.stroke-49")}),-1.0]])]});
            var Q7;
            Q7=makeQuery(id+"F22.imprint","IMPRINT",FACE,{"disambiguationData":[TD([[makeQuery(id+"F22.imprint","IMPRINT",EDGE,{"derivedFrom":sQuery(id+"F22.wireOp",EDGE,"E93.sketch_text.stroke-55")}),-1.0]])]});
            var Q8;
            Q8=makeQuery(id+"F22.imprint","IMPRINT",FACE,{"disambiguationData":[TD([[makeQuery(id+"F22.imprint","IMPRINT",EDGE,{"derivedFrom":sQuery(id+"F22.wireOp",EDGE,"E93.sketch_text.stroke-59")}),-1.0]])]});
            var Q9;
            Q9=makeQuery(id+"F22.imprint","IMPRINT",FACE,{"disambiguationData":[TD([[makeQuery(id+"F22.imprint","IMPRINT",EDGE,{"derivedFrom":sQuery(id+"F22.wireOp",EDGE,"E93.sketch_text.stroke-71")}),-1.0]])]});
            extrude(context, id + "F23", {"entities" : qUnion([Q0, Q1, Q2, Q3, Q4, Q5, Q6, Q7, Q8, Q9]), "operationType" : NewBodyOperationType.REMOVE, "oppositeDirection" : true, "depth" : 0.8 * mm, "offsetDistance" : 25.4 * mm});
        }
        {
            var Q0;
            {var subQ0=sQuery(id+"F2.wireOp",EDGE,"E1.4");Q0=makeQuery(id+"F4.boolean.opBoolean","MERGE",FACE,{"derivedFrom":[makeQuery(id+"F3.opExtrude","SWEPT_FACE",FACE,{"disambiguationData":[OSD([subQ0,sQuery(id+"F2.wireOp",EDGE,"E2.right")])]}),makeQuery(id+"F4.opExtrude","SWEPT_FACE",FACE,{"disambiguationData":[OSD([subQ0])]})]});}
            var sketch = newSketch(context, id + "F24", { "sketchPlane" : qUnion([Q0])});
            skLineSegment(sketch, "E94.bottom", {"start": v(28.57, 1162.05) * mm, "end": v(-28.57, 1162.05) * mm, "construction": true});
            skLineSegment(sketch, "E94.top", {"start": v(28.57, 1193.8) * mm, "end": v(-28.57, 1193.8) * mm, "construction": true});
            skLineSegment(sketch, "E94.left", {"start": v(28.57, 1162.05) * mm, "end": v(28.57, 1193.8) * mm, "construction": true});
            skLineSegment(sketch, "E94.right", {"start": v(-28.57, 1162.05) * mm, "end": v(-28.57, 1193.8) * mm, "construction": true});
            skPoint(sketch, "E94.middle", {"position": v(0, 1177.93) * mm});
            skLineSegment(sketch, "E95", {"start": v(0, 1193.8) * mm, "end": v(-28.57, 1177.93) * mm, "construction": true});
            skLineSegment(sketch, "E96", {"start": v(-28.57, 1177.93) * mm, "end": v(0, 1162.05) * mm, "construction": true});
            skLineSegment(sketch, "E97", {"start": v(0, 1162.05) * mm, "end": v(28.57, 1177.93) * mm, "construction": true});
            skLineSegment(sketch, "E98", {"start": v(28.57, 1177.93) * mm, "end": v(0, 1193.8) * mm, "construction": true});
            skLineSegment(sketch, "E99.bottom", {"start": v(24.29, 1173.07) * mm, "end": v(-24.29, 1173.07) * mm});
            skLineSegment(sketch, "E99.top", {"start": v(24.29, 1182.78) * mm, "end": v(-24.29, 1182.78) * mm});
            skLineSegment(sketch, "E99.left", {"start": v(24.29, 1173.07) * mm, "end": v(24.29, 1182.78) * mm});
            skLineSegment(sketch, "E99.right", {"start": v(-24.29, 1173.07) * mm, "end": v(-24.29, 1182.78) * mm});
            skLineSegment(sketch, "E100.bottom", {"start": v(25.87, 1171.49) * mm, "end": v(-25.87, 1171.49) * mm});
            skLineSegment(sketch, "E100.top", {"start": v(25.87, 1184.36) * mm, "end": v(-25.87, 1184.36) * mm});
            skLineSegment(sketch, "E100.left", {"start": v(25.87, 1171.49) * mm, "end": v(25.87, 1184.36) * mm});
            skLineSegment(sketch, "E100.right", {"start": v(-25.87, 1171.49) * mm, "end": v(-25.87, 1184.36) * mm});
            skPoint(sketch, "E101.sketch_text.left.end.orphan", {"position": v(-22.7, 1181.19) * mm});
            skText(sketch, "E102", { "text": "ARTILLIER", "fontName": "OpenSans-Bold.ttf"});
            const initialGuessF24  = {"E102": [-0.02243, 1.17481, 1, 0, 0.00653]};
            skSetInitialGuess(sketch, initialGuessF24);
            skSolve(sketch);
        }
        {
            var Q0;
            Q0=makeQuery(id+"F24.imprint","IMPRINT",FACE,{"disambiguationData":[TD([[makeQuery(id+"F24.imprint","IMPRINT",EDGE,{"derivedFrom":sQuery(id+"F24.wireOp",EDGE,"E99.bottom")}),1.0]])]});
            var Q1;
            Q1=makeQuery(id+"F24.imprint","IMPRINT",FACE,{"disambiguationData":[TD([[makeQuery(id+"F24.imprint","IMPRINT",EDGE,{"derivedFrom":sQuery(id+"F24.wireOp",EDGE,"E102.sketch_text.stroke-0")}),-1.0]])]});
            var Q2;
            Q2=makeQuery(id+"F24.imprint","IMPRINT",FACE,{"disambiguationData":[TD([[makeQuery(id+"F24.imprint","IMPRINT",EDGE,{"derivedFrom":sQuery(id+"F24.wireOp",EDGE,"E102.sketch_text.stroke-12")}),-1.0]])]});
            var Q3;
            Q3=makeQuery(id+"F24.imprint","IMPRINT",FACE,{"disambiguationData":[TD([[makeQuery(id+"F24.imprint","IMPRINT",EDGE,{"derivedFrom":sQuery(id+"F24.wireOp",EDGE,"E102.sketch_text.stroke-39")}),-1.0]])]});
            var Q4;
            Q4=makeQuery(id+"F24.imprint","IMPRINT",FACE,{"disambiguationData":[TD([[makeQuery(id+"F24.imprint","IMPRINT",EDGE,{"derivedFrom":sQuery(id+"F24.wireOp",EDGE,"E102.sketch_text.stroke-43")}),-1.0]])]});
            var Q5;
            Q5=makeQuery(id+"F24.imprint","IMPRINT",FACE,{"disambiguationData":[TD([[makeQuery(id+"F24.imprint","IMPRINT",EDGE,{"derivedFrom":sQuery(id+"F24.wireOp",EDGE,"E102.sketch_text.stroke-31")}),-1.0]])]});
            var Q6;
            Q6=makeQuery(id+"F24.imprint","IMPRINT",FACE,{"disambiguationData":[TD([[makeQuery(id+"F24.imprint","IMPRINT",EDGE,{"derivedFrom":sQuery(id+"F24.wireOp",EDGE,"E102.sketch_text.stroke-55")}),-1.0]])]});
            var Q7;
            Q7=makeQuery(id+"F24.imprint","IMPRINT",FACE,{"disambiguationData":[TD([[makeQuery(id+"F24.imprint","IMPRINT",EDGE,{"derivedFrom":sQuery(id+"F24.wireOp",EDGE,"E102.sketch_text.stroke-59")}),-1.0]])]});
            var Q8;
            Q8=makeQuery(id+"F24.imprint","IMPRINT",FACE,{"disambiguationData":[TD([[makeQuery(id+"F24.imprint","IMPRINT",EDGE,{"derivedFrom":sQuery(id+"F24.wireOp",EDGE,"E102.sketch_text.stroke-71")}),-1.0]])]});
            var Q9;
            Q9=makeQuery(id+"F24.imprint","IMPRINT",FACE,{"disambiguationData":[TD([[makeQuery(id+"F24.imprint","IMPRINT",EDGE,{"derivedFrom":sQuery(id+"F24.wireOp",EDGE,"E102.sketch_text.stroke-49")}),-1.0]])]});
            extrude(context, id + "F25", {"entities" : qUnion([Q0, Q1, Q2, Q3, Q4, Q5, Q6, Q7, Q8, Q9]), "operationType" : NewBodyOperationType.REMOVE, "oppositeDirection" : true, "depth" : 0.8 * mm, "offsetDistance" : 25.4 * mm});
        }
        {
            var Q0;
            Q0=qCreatedBy(makeId("Right.planeOp"),FACE);
            var sketch = newSketch(context, id + "F26", { "sketchPlane" : qUnion([Q0])});
            skCircle(sketch, "E103.cCircle", {"center": v(44.45, 1177.93) * mm, "radius": 6.19 * mm, "construction": true});
            skLineSegment(sketch, "E103.0", {"start": v(51.6, 1177.92) * mm, "end": v(48.02, 1171.74) * mm});
            skLineSegment(sketch, "E103.1", {"start": v(48.02, 1171.74) * mm, "end": v(40.88, 1171.74) * mm});
            skLineSegment(sketch, "E103.2", {"start": v(40.88, 1171.74) * mm, "end": v(37.3, 1177.93) * mm});
            skLineSegment(sketch, "E103.3", {"start": v(37.3, 1177.93) * mm, "end": v(40.88, 1184.11) * mm});
            skLineSegment(sketch, "E103.4", {"start": v(40.88, 1184.11) * mm, "end": v(48.02, 1184.11) * mm});
            skLineSegment(sketch, "E103.5", {"start": v(48.02, 1184.11) * mm, "end": v(51.6, 1177.93) * mm});
            skPoint(sketch, "E103.0.midPoint", {"position": v(49.8, 1174.83) * mm});
            skCircle(sketch, "E104.cCircle", {"center": v(69.85, 1177.93) * mm, "radius": 6.19 * mm, "construction": true});
            skLineSegment(sketch, "E104.0", {"start": v(73.42, 1171.74) * mm, "end": v(66.28, 1171.74) * mm});
            skLineSegment(sketch, "E104.1", {"start": v(66.28, 1171.74) * mm, "end": v(62.7, 1177.93) * mm});
            skLineSegment(sketch, "E104.2", {"start": v(62.7, 1177.93) * mm, "end": v(66.28, 1184.11) * mm});
            skLineSegment(sketch, "E104.3", {"start": v(66.28, 1184.11) * mm, "end": v(73.42, 1184.11) * mm});
            skLineSegment(sketch, "E104.4", {"start": v(73.42, 1184.11) * mm, "end": v(77, 1177.93) * mm});
            skLineSegment(sketch, "E104.5", {"start": v(77, 1177.93) * mm, "end": v(73.42, 1171.74) * mm});
            skPoint(sketch, "E104.0.midPoint", {"position": v(69.85, 1171.74) * mm});
            skCircle(sketch, "E105", {"center": v(44.45, 1177.93) * mm, "radius": 4.76 * mm});
            skCircle(sketch, "E106", {"center": v(69.85, 1177.93) * mm, "radius": 4.76 * mm});
            skSolve(sketch);
        }
        {
            var Q0;
            Q0 = qSketchRegion(id + "F26", true);
            extrude(context, id + "F27", {"entities" : qUnion([Q0]), "operationType" : NewBodyOperationType.ADD, "depth" : 38.1 * mm, "offsetDistance" : 25.4 * mm, "hasSecondDirection" : true, "secondDirectionOppositeDirection" : true, "secondDirectionDepth" : 38.1 * mm});
        }
        {
            var Q0;
            Q0=makeQuery(id+"F26.imprint","IMPRINT",FACE,{"disambiguationData":[TD([[makeQuery(id+"F26.imprint","IMPRINT",EDGE,{"derivedFrom":sQuery(id+"F26.wireOp",EDGE,"E105")}),1.0]])]});
            var Q1;
            Q1=makeQuery(id+"F26.imprint","IMPRINT",FACE,{"disambiguationData":[TD([[makeQuery(id+"F26.imprint","IMPRINT",EDGE,{"derivedFrom":sQuery(id+"F26.wireOp",EDGE,"E106")}),1.0]])]});
            extrude(context, id + "F28", {"entities" : qUnion([Q0, Q1]), "operationType" : NewBodyOperationType.ADD, "depth" : 47.62 * mm, "offsetDistance" : 25.4 * mm, "hasSecondDirection" : true, "secondDirectionOppositeDirection" : true, "secondDirectionDepth" : 47.62 * mm});
        }
    });
